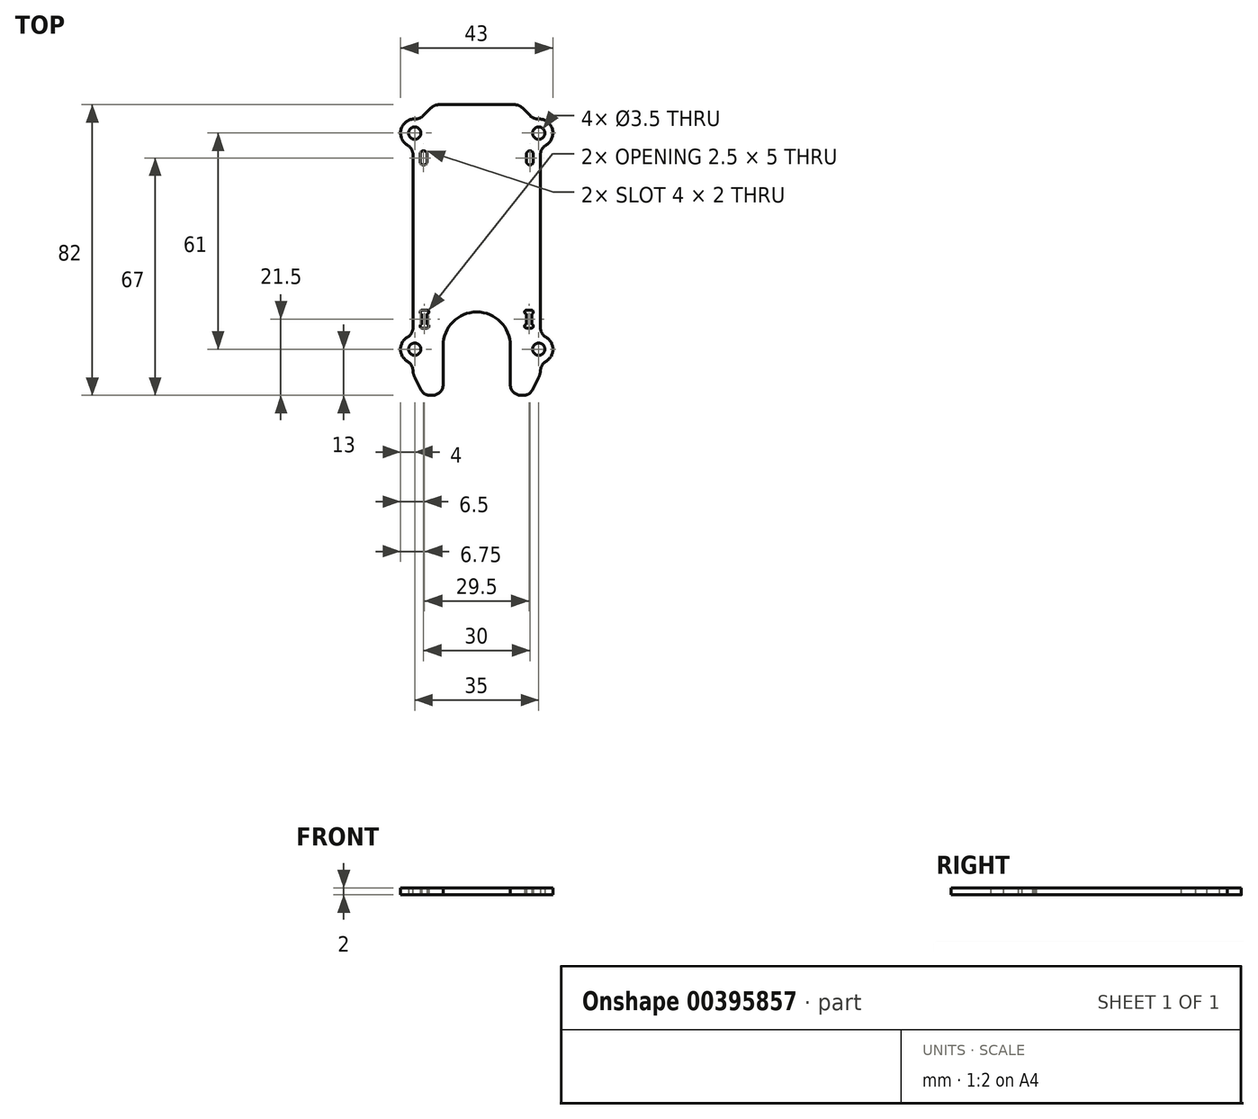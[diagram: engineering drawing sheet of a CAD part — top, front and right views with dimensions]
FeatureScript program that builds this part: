
annotation { "Feature Type Name" : "Feature", "Feature Type Description" : "" }
export const myFeature = defineFeature(function(context is Context, id is Id, definition is map)
    precondition{}
    {
        {
            var Q0;
            Q0=qCreatedBy(makeId("Top.planeOp"),FACE);
            var sketch = newSketch(context, id + "F0", { "sketchPlane" : qUnion([Q0])});
            skLineSegment(sketch, "E0.top", {"start": v(-13.15, -49) * mm, "end": v(-12.5, -49) * mm});
            skLineSegment(sketch, "E0.left", {"start": v(-18, 21.03) * mm, "end": v(-18, -32.03) * mm});
            skCircle(sketch, "E1", {"center": v(-15.25, 15.25) * mm, "radius": 1.75 * mm, "construction": true});
            skCircle(sketch, "E2", {"center": v(-15.25, -15.25) * mm, "radius": 1.75 * mm, "construction": true});
            skCircle(sketch, "E3.MirrorC", {"center": v(15.25, 15.25) * mm, "radius": 1.75 * mm, "construction": true});
            skCircle(sketch, "E4.MirrorC", {"center": v(15.25, -15.25) * mm, "radius": 1.75 * mm, "construction": true});
            skCircle(sketch, "E5", {"center": v(-17.5, -36) * mm, "radius": 1.75 * mm});
            skCircle(sketch, "E6.MirrorC", {"center": v(17.5, -36) * mm, "radius": 1.75 * mm});
            skLineSegment(sketch, "E7", {"start": v(0, 0) * mm, "end": v(74.25, -74.25) * mm, "construction": true});
            skLineSegment(sketch, "E8", {"start": v(0, 0) * mm, "end": v(74.25, 74.25) * mm, "construction": true});
            skLineSegment(sketch, "E9", {"start": v(0, 0) * mm, "end": v(-74.25, 74.25) * mm, "construction": true});
            skLineSegment(sketch, "E10", {"start": v(0, 0) * mm, "end": v(-74.25, -74.25) * mm, "construction": true});
            skCircle(sketch, "E11", {"center": v(0, 0) * mm, "radius": 105 * mm, "construction": true});
            skCircle(sketch, "E12", {"center": v(74.25, -74.25) * mm, "radius": 63.5 * mm, "construction": true});
            skLineSegment(sketch, "E13", {"start": v(17.47, -44.06) * mm, "end": v(15.83, -47.34) * mm});
            skLineSegment(sketch, "E14.MirrorCS", {"start": v(-17.47, -44.06) * mm, "end": v(-15.83, -47.34) * mm});
            skLineSegment(sketch, "E15", {"start": v(-9.5, -46) * mm, "end": v(-9.5, -35) * mm});
            skLineSegment(sketch, "E16", {"start": v(9.5, -46) * mm, "end": v(9.5, -35) * mm});
            skLineSegment(sketch, "E17.trimOffspring", {"start": v(12.5, -49) * mm, "end": v(13.15, -49) * mm});
            skPoint(sketch, "E18.visualSharp", {"position": v(-18, -43) * mm});
            skArc(sketch, "E18.filletArc", {"start": v(-18, -41.82) * mm, "mid": v(-17.87, -42.97) * mm, "end": v(-17.47, -44.06) * mm});
            skPoint(sketch, "E19.visualSharp", {"position": v(18, -43) * mm});
            skArc(sketch, "E19.filletArc", {"start": v(17.47, -44.06) * mm, "mid": v(17.87, -42.97) * mm, "end": v(18, -41.82) * mm});
            skPoint(sketch, "E20.visualSharp", {"position": v(-9.5, -49) * mm});
            skArc(sketch, "E20.filletArc", {"start": v(-12.5, -49) * mm, "mid": v(-10.38, -48.12) * mm, "end": v(-9.5, -46) * mm});
            skPoint(sketch, "E21.visualSharp", {"position": v(-15, -49) * mm});
            skArc(sketch, "E21.filletArc", {"start": v(-15.83, -47.34) * mm, "mid": v(-14.72, -48.55) * mm, "end": v(-13.15, -49) * mm});
            skPoint(sketch, "E22.visualSharp", {"position": v(15, -49) * mm});
            skArc(sketch, "E22.filletArc", {"start": v(13.15, -49) * mm, "mid": v(14.72, -48.55) * mm, "end": v(15.83, -47.34) * mm});
            skPoint(sketch, "E23.visualSharp", {"position": v(9.5, -49) * mm});
            skArc(sketch, "E23.filletArc", {"start": v(9.5, -46) * mm, "mid": v(10.38, -48.12) * mm, "end": v(12.5, -49) * mm});
            skLineSegment(sketch, "E24", {"start": v(-10.76, 33) * mm, "end": v(10.76, 33) * mm});
            skLineSegment(sketch, "E25", {"start": v(-16.21, 28.79) * mm, "end": v(-12.88, 32.12) * mm});
            skLineSegment(sketch, "E26", {"start": v(12.88, 32.12) * mm, "end": v(16.21, 28.79) * mm});
            skPoint(sketch, "E27.visualSharp", {"position": v(-12, 33) * mm});
            skArc(sketch, "E27.filletArc", {"start": v(-10.76, 33) * mm, "mid": v(-11.9, 32.77) * mm, "end": v(-12.88, 32.12) * mm});
            skPoint(sketch, "E28.visualSharp", {"position": v(12, 33) * mm});
            skArc(sketch, "E28.filletArc", {"start": v(12.88, 32.12) * mm, "mid": v(11.9, 32.77) * mm, "end": v(10.76, 33) * mm});
            skPoint(sketch, "E29.visualSharp", {"position": v(-18, 27) * mm});
            skCircle(sketch, "E30", {"center": v(-17.5, 25) * mm, "radius": 1.75 * mm});
            skCircle(sketch, "E31.MirrorC", {"center": v(17.5, 25) * mm, "radius": 1.75 * mm});
            skArc(sketch, "E32", {"start": v(9.5, -35) * mm, "mid": v(0, -25.5) * mm, "end": v(-9.5, -35) * mm});
            skLineSegment(sketch, "E33.bottom", {"start": v(-15.5, -25) * mm, "end": v(-14, -25) * mm});
            skLineSegment(sketch, "E33.top", {"start": v(-15.5, -30) * mm, "end": v(-14, -30) * mm});
            skLineSegment(sketch, "E33.left", {"start": v(-15.5, -26) * mm, "end": v(-15.5, -29) * mm});
            skLineSegment(sketch, "E33.right", {"start": v(-14, -26) * mm, "end": v(-14, -29) * mm});
            skArc(sketch, "E34", {"start": v(-15.5, -25) * mm, "mid": v(-16, -25.5) * mm, "end": v(-15.5, -26) * mm});
            skArc(sketch, "E35", {"start": v(-14, -26) * mm, "mid": v(-13.5, -25.5) * mm, "end": v(-14, -25) * mm});
            skArc(sketch, "E36", {"start": v(-15.5, -29) * mm, "mid": v(-16, -29.5) * mm, "end": v(-15.5, -30) * mm});
            skArc(sketch, "E37", {"start": v(-14, -30) * mm, "mid": v(-13.5, -29.5) * mm, "end": v(-14, -29) * mm});
            skArc(sketch, "E38.MirrorCS", {"start": v(14, -30) * mm, "mid": v(13.5, -29.5) * mm, "end": v(14, -29) * mm});
            skArc(sketch, "E39.MirrorCS", {"start": v(15.5, -29) * mm, "mid": v(16, -29.5) * mm, "end": v(15.5, -30) * mm});
            skLineSegment(sketch, "E40.MirrorCS", {"start": v(15.5, -30) * mm, "end": v(14, -30) * mm});
            skLineSegment(sketch, "E41.MirrorCS", {"start": v(15.5, -26) * mm, "end": v(15.5, -29) * mm});
            skArc(sketch, "E42.MirrorCS", {"start": v(14, -26) * mm, "mid": v(13.5, -25.5) * mm, "end": v(14, -25) * mm});
            skArc(sketch, "E43.MirrorCS", {"start": v(15.5, -25) * mm, "mid": v(16, -25.5) * mm, "end": v(15.5, -26) * mm});
            skLineSegment(sketch, "E44.MirrorCS", {"start": v(15.5, -25) * mm, "end": v(14, -25) * mm});
            skLineSegment(sketch, "E45.MirrorCS", {"start": v(14, -26) * mm, "end": v(14, -29) * mm});
            skLineSegment(sketch, "E46", {"start": v(-15, 19) * mm, "end": v(-15, 17) * mm, "construction": true});
            skArc(sketch, "E47.0.startCap", {"start": v(-16, 19) * mm, "mid": v(-15, 20) * mm, "end": v(-14, 19) * mm});
            skArc(sketch, "E47.0.endCap", {"start": v(-14, 17) * mm, "mid": v(-15, 16) * mm, "end": v(-16, 17) * mm});
            skLineSegment(sketch, "E47.0.left", {"start": v(-14, 19) * mm, "end": v(-14, 17) * mm});
            skLineSegment(sketch, "E47.0.right", {"start": v(-16, 19) * mm, "end": v(-16, 17) * mm});
            skLineSegment(sketch, "E48.MirrorCS", {"start": v(16, 19) * mm, "end": v(16, 17) * mm});
            skLineSegment(sketch, "E49.MirrorCS", {"start": v(14, 19) * mm, "end": v(14, 17) * mm});
            skLineSegment(sketch, "E50.MirrorCS", {"start": v(15, 19) * mm, "end": v(15, 17) * mm, "construction": true});
            skArc(sketch, "E51.MirrorCS", {"start": v(14, 17) * mm, "mid": v(15, 16) * mm, "end": v(16, 17) * mm});
            skArc(sketch, "E52.MirrorCS", {"start": v(16, 19) * mm, "mid": v(15, 20) * mm, "end": v(14, 19) * mm});
            skArc(sketch, "E53", {"start": v(-18, -32.03) * mm, "mid": v(-21.5, -36) * mm, "end": v(-18, -39.97) * mm});
            skLineSegment(sketch, "E54.trimOffspring", {"start": v(-18, -39.97) * mm, "end": v(-18, -41.82) * mm});
            skArc(sketch, "E55.MirrorCS", {"start": v(18, -32.03) * mm, "mid": v(21.5, -36) * mm, "end": v(18, -39.97) * mm});
            skLineSegment(sketch, "E56.trimOffspring", {"start": v(18, -39.97) * mm, "end": v(18, -41.82) * mm});
            skArc(sketch, "E57", {"start": v(-16.21, 28.79) * mm, "mid": v(-21.4, 25.9) * mm, "end": v(-18, 21.03) * mm});
            skArc(sketch, "E58.MirrorCS", {"start": v(16.21, 28.79) * mm, "mid": v(21.4, 25.9) * mm, "end": v(18, 21.03) * mm});
            skLineSegment(sketch, "E59.trimOffspring", {"start": v(18, 21.03) * mm, "end": v(18, -32.03) * mm});
            skSolve(sketch);
        }
        {
            var Q0;
            Q0 = qSketchRegion(id + "F0", true);
            extrude(context, id + "F1", {"entities" : qUnion([Q0]), "depth" : 2 * mm});
        }
        {
            var Q0;
            Q0=makeQuery(id+"F1.opExtrude","SWEPT_EDGE",EDGE,{"disambiguationData":[OSD([sQuery(id+"F0.wireOp",EDGE,"E53"),sQuery(id+"F0.wireOp",EDGE,"E54.trimOffspring")])]});
            var Q1;
            Q1=makeQuery(id+"F1.opExtrude","SWEPT_EDGE",EDGE,{"disambiguationData":[OSD([sQuery(id+"F0.wireOp",EDGE,"E0.left"),sQuery(id+"F0.wireOp",EDGE,"E53")])]});
            var Q2;
            Q2=makeQuery(id+"F1.opExtrude","SWEPT_EDGE",EDGE,{"disambiguationData":[OSD([sQuery(id+"F0.wireOp",EDGE,"E55.MirrorCS"),sQuery(id+"F0.wireOp",EDGE,"E56.trimOffspring")])]});
            var Q3;
            Q3=makeQuery(id+"F1.opExtrude","SWEPT_EDGE",EDGE,{"disambiguationData":[OSD([sQuery(id+"F0.wireOp",EDGE,"E55.MirrorCS"),sQuery(id+"F0.wireOp",EDGE,"E59.trimOffspring")])]});
            var Q4;
            Q4=makeQuery(id+"F1.opExtrude","SWEPT_EDGE",EDGE,{"disambiguationData":[OSD([sQuery(id+"F0.wireOp",EDGE,"E26"),sQuery(id+"F0.wireOp",EDGE,"E58.MirrorCS")])]});
            var Q5;
            Q5=makeQuery(id+"F1.opExtrude","SWEPT_EDGE",EDGE,{"disambiguationData":[OSD([sQuery(id+"F0.wireOp",EDGE,"E58.MirrorCS"),sQuery(id+"F0.wireOp",EDGE,"E59.trimOffspring")])]});
            var Q6;
            Q6=makeQuery(id+"F1.opExtrude","SWEPT_EDGE",EDGE,{"disambiguationData":[OSD([sQuery(id+"F0.wireOp",EDGE,"E25"),sQuery(id+"F0.wireOp",EDGE,"E57")])]});
            var Q7;
            Q7=makeQuery(id+"F1.opExtrude","SWEPT_EDGE",EDGE,{"disambiguationData":[OSD([sQuery(id+"F0.wireOp",EDGE,"E0.left"),sQuery(id+"F0.wireOp",EDGE,"E57")])]});
            fillet(context, id + "F2", {"entities" : qUnion([Q0, Q1, Q2, Q3, Q4, Q5, Q6, Q7]), "radius" : 3 * mm, "tangentPropagation" : true, "allowEdgeOverflow" : false});
        }
    });
